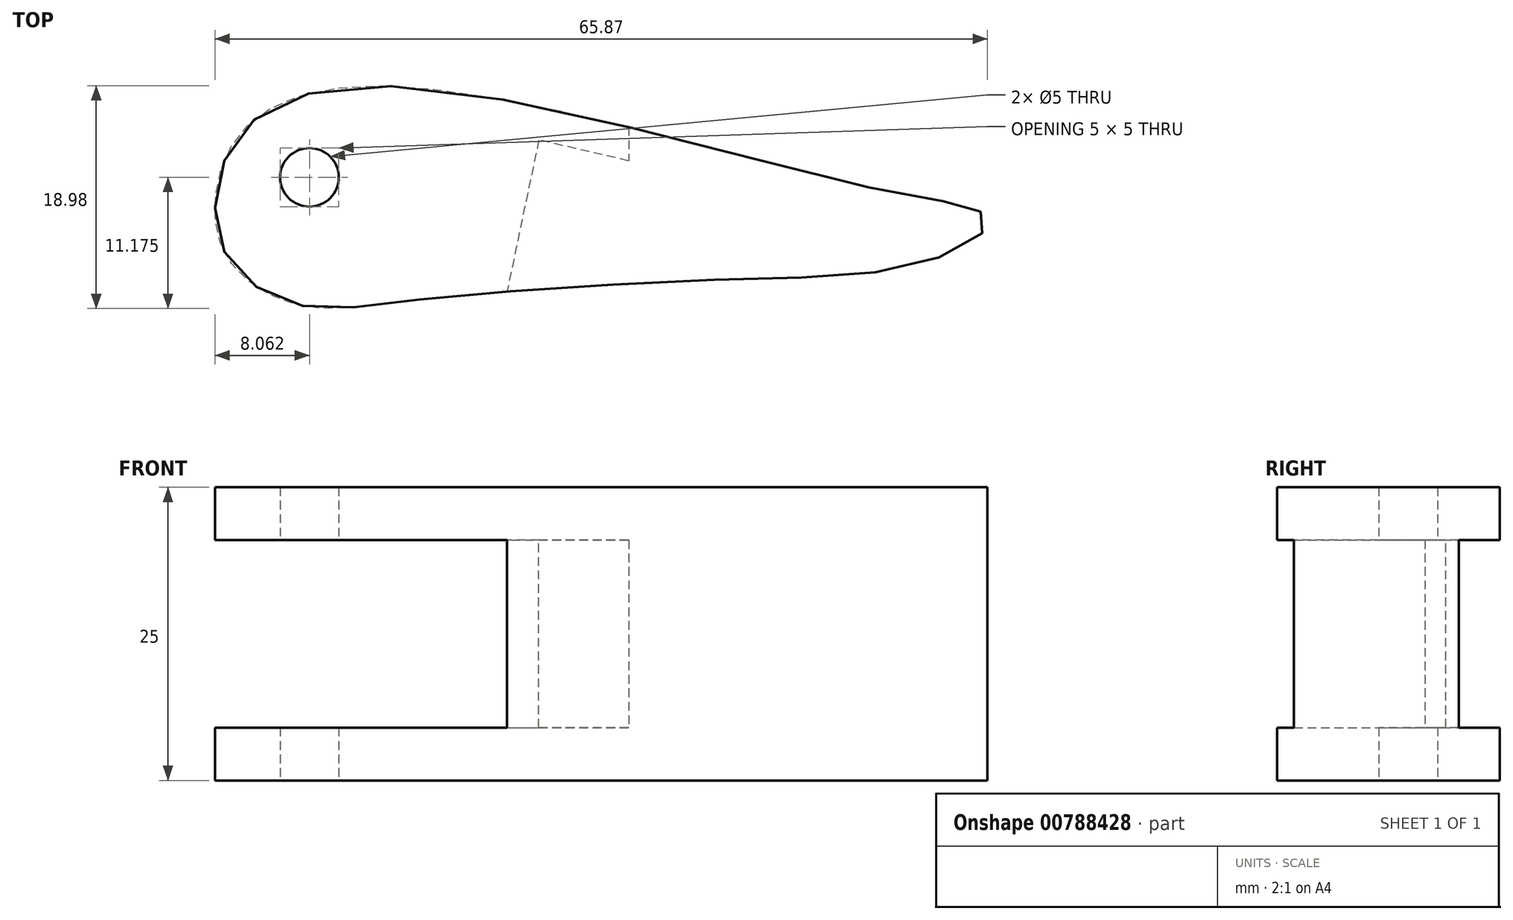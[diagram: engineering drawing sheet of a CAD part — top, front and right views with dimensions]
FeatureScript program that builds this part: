
annotation { "Feature Type Name" : "Feature", "Feature Type Description" : "" }
export const myFeature = defineFeature(function(context is Context, id is Id, definition is map)
    precondition{}
    {
        {
            var Q0;
            Q0=qCreatedBy(makeId("Top.planeOp"),FACE);
            var sketch = newSketch(context, id + "F0", { "sketchPlane" : qUnion([Q0])});
            skFitSpline(sketch, "E0", {"points": [v(33.2, 11.36) * mm, v(33.7, 10.07) * mm, v(27.74, 6.87) * mm, v(11.07, 5.56) * mm, v(-15.77, 3.74) * mm, v(-24.91, 3.38) * mm, v(-30.67, 6.92) * mm, v(-32.05, 12.49) * mm, v(-29.3, 18.7) * mm, v(-15.36, 21.98) * mm, v(25.65, 13) * mm, v(33.2, 11.36) * mm]});
            skCircle(sketch, "E1", {"center": v(-24.03, 14.28) * mm, "radius": 2.5 * mm});
            skSolve(sketch);
        }
        {
            var Q0;
            Q0=makeQuery(id+"F0.imprint","IMPRINT",FACE,{"disambiguationData":[TD([[makeQuery(id+"F0.imprint","IMPRINT",EDGE,{"derivedFrom":sQuery(id+"F0.wireOp",EDGE,"E0")}),-1.0]])]});
            extrude(context, id + "F1", {"entities" : qUnion([Q0]), "depth" : 25 * mm, "offsetDistance" : 25 * mm});
        }
        {
            var Q0;
            Q0=qCreatedBy(makeId("Front.planeOp"),FACE);
            var sketch = newSketch(context, id + "F2", { "sketchPlane" : qUnion([Q0])});
            skLineSegment(sketch, "E2.bottom", {"start": v(-32.23, 20.5) * mm, "end": v(-7.23, 20.5) * mm});
            skLineSegment(sketch, "E2.top", {"start": v(-32.23, 4.5) * mm, "end": v(-7.23, 4.5) * mm});
            skLineSegment(sketch, "E2.left", {"start": v(-32.23, 20.5) * mm, "end": v(-32.23, 4.5) * mm});
            skLineSegment(sketch, "E2.right", {"start": v(-7.23, 20.5) * mm, "end": v(-7.23, 4.5) * mm});
            skPoint(sketch, "E2.middle", {"position": v(-19.73, 12.5) * mm});
            skSolve(sketch);
        }
        {
            var Q0;
            Q0=makeQuery(id+"F2.imprint","IMPRINT",FACE,{"disambiguationData":[TD([[makeQuery(id+"F2.imprint","IMPRINT",EDGE,{"derivedFrom":sQuery(id+"F2.wireOp",EDGE,"E2.bottom")}),-1.0]])]});
            extrude(context, id + "F3", {"entities" : qUnion([Q0]), "operationType" : NewBodyOperationType.REMOVE, "oppositeDirection" : true, "depth" : 25 * mm, "offsetDistance" : 25 * mm});
        }
        {
            var Q0;
            Q0=makeQuery(id+"F3.boolean.opBoolean","INTERSECT",EDGE,{"disambiguationData":[OD(1.0)],"derivedFrom":[makeQuery(id+"F1.opExtrude","SWEPT_FACE",FACE,{"disambiguationData":[OSD([sQuery(id+"F0.wireOp",EDGE,"E0")])]}),makeQuery(id+"F3.opExtrude","SWEPT_FACE",FACE,{"disambiguationData":[OSD([sQuery(id+"F2.wireOp",EDGE,"E2.right")])]})]});
            chamfer(context, id + "F4", {"entities" : qUnion([Q0]), "chamferType" : ChamferType.TWO_OFFSETS, "width1" : 3 * mm, "oppositeDirection" : false, "width2" : 16.5 * mm, "tangentPropagation" : true});
        }
        {
            var Q0;
            Q0=qCreatedBy(makeId("Top.planeOp"),FACE);
            cPlane(context, id + "F5", {"entities" : qUnion([Q0]), "cplaneType" : CPlaneType.OFFSET, "offset" : 4.5 * mm, "width" : 150 * mm, "height" : 150 * mm});
        }
        {
            var Q0;
            Q0=qCreatedBy(id+"F5.planeOp",FACE);
            var sketch = newSketch(context, id + "F6", { "sketchPlane" : qUnion([Q0])});
            skLineSegment(sketch, "E3", {"start": v(-4.6, 20.5) * mm, "end": v(3.19, 18.7) * mm});
            skLineSegment(sketch, "E4", {"start": v(3.19, 18.7) * mm, "end": v(3.19, 15.7) * mm});
            skLineSegment(sketch, "E5", {"start": v(3.19, 15.7) * mm, "end": v(-4.6, 17.5) * mm});
            skLineSegment(sketch, "E6", {"start": v(-4.6, 17.5) * mm, "end": v(-4.6, 20.5) * mm});
            skSolve(sketch);
        }
        {
            var Q0;
            Q0 = qSketchRegion(id + "F6", true);
            extrude(context, id + "F7", {"entities" : qUnion([Q0]), "operationType" : NewBodyOperationType.REMOVE, "depth" : 16 * mm, "offsetDistance" : 25 * mm});
        }
    });
